# Revit family: ENCBHTYP009
name_source: partatom
category: Furniture
units: mm (PartAtom-declared; Revit-internal decimal feet)

## family parameters
Always vertical = Yes
Cut with Voids When Loaded = No
OmniClass Number = 23.40.20.00
OmniClass Title = General Furniture and Specialties
Render Appearance Source = Family Geometry
Room Calculation Point = No
Shared = No
Work Plane-Based = No

## types (1)
- ENCBHTYP009
    Cost = 36058 $
    Default Elevation = 0 mm  [stored 0 ft]
    Description = 2 x Pass Thru Jumper 30W Panel - 39L - 8 wire, 4 circuit, 3 x Black Duplex Outlet - Line 1, 3 x Black Duplex Outlet - Line 2, 3 x Black Duplex Outlet - Line 3, 3 x Black Duplex Outlet - Line 4, 1 x Side Mounted Base Infeed - 72L - 8 Wire, 4 Circuit, 3 x Slimline Scrn,Uni Spine,FVWL,Dim A,SpnMntUni,20hx60w, 6 x Encounter PwrBench HAT 2Leg, Dbl Sided,Sq Edge,Scallop,30x60, 7 x Encounter PwrBeam Beam Spine Connection Kit, H Leg Only, 3 x Encounter PwrBeam Powered Spine Kit 60, 6 x Encounter PwrBeam Power Cord Tray 60w, 2 x Encounter PwrBeam Raceway Endcap Painted, 1 x Encounter PwrBeam UnderMnt pole for 29h, 6 x Encounter PwrBench H-Leg Double-Sided
    Exported From CET Designer = Yes
    Manufacturer = AIS
    Model = E-HM8W4PJ30
    Show ENCBHTYP009 = Yes
    VisibilityIndex = 0

note: [stored X ft] marks values corroborated as IEEE doubles in the binary element streams (Revit-internal decimal feet)

## geometry (parser evidence)
native form markers: Sweep x3
no freeform markers — native parametric forms only
